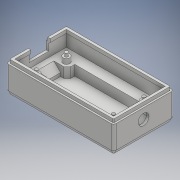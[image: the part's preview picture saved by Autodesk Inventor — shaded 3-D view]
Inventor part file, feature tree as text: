
AUTODESK INVENTOR PART (.ipt)
format: ipt  version: 2018.3 (Build 223284000, 284)  size: 285,184 bytes
history: native  units: mm
features: extrude x11, sketch x11, projected_geometry x5, chamfer x4, fillet x1
ambient origin geometry x8: Origin, YZ Plane, XZ Plane, XY Plane, X Axis, Y Axis, Z Axis, Center Point
bodies: Solid1 (feature_tree)
feature tree (32):
  extrude  "Extrusion1"  Depth=35.56mm
  extrude  "Extrusion2"  Depth=16.2mm TaperAngle=0.0deg
  extrude  "Extrusion3"  Depth=38.0mm
  extrude  "Extrusion4"  Depth=6.28mm
  extrude  "Extrusion5"  Depth=11.25mm
  fillet  "Fillet1"  Radius=60.5mm
  extrude  "Extrusion6"  Depth=2.0mm
  extrude  "Extrusion7"  Depth=2.0mm
  extrude  "Extrusion8"  Depth=2.0mm
  chamfer  "Chamfer1"  Distance=32.56mm
  chamfer  "Chamfer2"  Distance=60.5mm
  extrude  "Extrusion9"  Depth=2.0mm
  chamfer  "Chamfer3"  [1 undecoded]
  extrude  "Extrusion10"  Depth=5.0mm TaperAngle=0.0deg
  extrude  "Extrusion11"  Depth=1.0mm
  chamfer  "Chamfer4"  Distance=1.0mm
  sketch  "Sketch1"  dims[d0=63.5mm d1=35.56mm]
  sketch  "Sketch2"  dims[d2=1.5mm d3=16.2mm d4=0.0mm]
  sketch  "Sketch3"  dims[d5=1.5mm d6=0.0mm d7=38.0mm]
  projected_geometry  "Projected Loop1"
  sketch  "Sketch4"  dims[d8=20.0mm d9=6.28mm]
  sketch  "Sketch5"  dims[d10=32.56mm d11=11.25mm d12=60.5mm]
  projected_geometry  "Projected Loop2"
  projected_geometry  "Projected Loop3"
  projected_geometry  "Projected Loop4"
  projected_geometry  "Projected Loop5"
  sketch  "Sketch6"  dims[d13=6.0mm d14=0.0mm d15=2.0mm]
  sketch  "Sketch7"  dims[d16=2.0mm d17=2.0mm]
  sketch  "Sketch8"  dims[d18=2.0mm d19=45.72mm]
  sketch  "Sketch9"  dims[d20=45.72mm]
  sketch  "Sketch10"  dims[d21=17.78mm]
  sketch  "Sketch11"  dims[d22=7.39mm d23=32.56mm d24=60.5mm d25=7.39mm d26=0.0mm d27=5.0mm d28=0.0mm d29=1.0mm d30=1.0mm d31=1.0mm d32=1.0mm d33=3.0mm d34=0.0mm d35=1.5mm d36=6.4mm d37=8.0mm d38=17.78mm d39=35.56mm d40=3.0mm d41=0.0mm d42=11.0mm d43=3.0mm d44=0.0mm d45=3.0mm d46=0.0mm d47=2.0mm d48=2.0mm d49=45.0deg d50=4.0mm d51=2.0mm d52=45.0deg d53=1.0mm d54=3.0mm d55=0.0mm d56=1.0mm d57=2.0mm d58=45.0deg d59=1.0mm d60=2.0mm d61=0.0mm d62=12.0mm d63=12.0mm d64=7.0mm d65=2.2mm d66=0.0mm d67=1.0mm d68=2.0mm d69=45.0deg]
note: 1 required parameter value undecoded (feature->parameter linkage not recoverable at this tier; creation-order binding heuristic only, values carry confidence <= 0.55)
